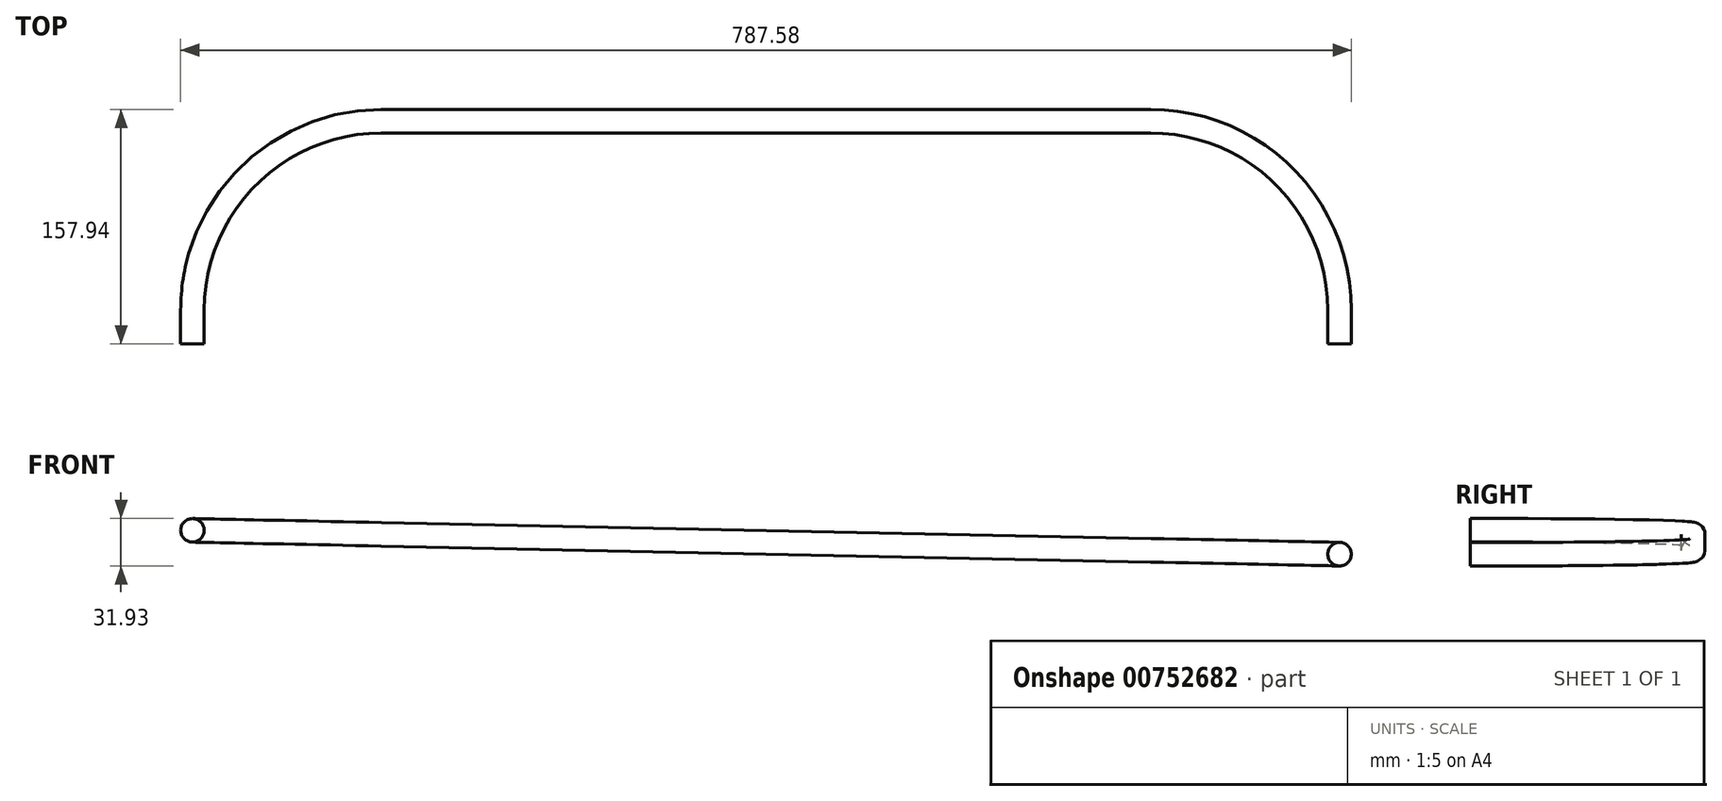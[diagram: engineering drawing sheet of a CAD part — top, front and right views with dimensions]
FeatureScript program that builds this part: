
annotation { "Feature Type Name" : "Feature", "Feature Type Description" : "" }
export const myFeature = defineFeature(function(context is Context, id is Id, definition is map)
    precondition{}
    {
        {
            var Q0;
            Q0=qCreatedBy(makeId("Front.planeOp"),FACE);
            var sketch = newSketch(context, id + "F0", { "sketchPlane" : qUnion([Q0])});
            skLineSegment(sketch, "E0", {"start": v(0, 0) * mm, "end": v(-771.7, 0) * mm, "construction": true});
            skLineSegment(sketch, "E1", {"start": v(-771.7, 0) * mm, "end": v(-771.7, 16.05) * mm, "construction": true});
            skPoint(sketch, "E2", {"position": v(-771.7, 16.05) * mm});
            skLineSegment(sketch, "E3", {"start": v(0, 0) * mm, "end": v(-771.7, 16.05) * mm});
            skSolve(sketch);
        }
        {
            var Q0;
            Q0=qCreatedBy(makeId("Top.planeOp"),FACE);
            var sketch = newSketch(context, id + "F1", { "sketchPlane" : qUnion([Q0])});
            skLineSegment(sketch, "E4", {"start": v(0, 0) * mm, "end": v(0, -50) * mm});
            skSolve(sketch);
        }
        {
            var Q0;
            Q0=sQuery(id+"F1.wireOp",VERTEX,"E4.end");
            var Q1;
            Q1=sQuery(id+"F0.wireOp",VERTEX,"E0.start");
            var Q2;
            Q2=sQuery(id+"F0.wireOp",VERTEX,"E2");
            cPlane(context, id + "F2", {"entities" : qUnion([Q0, Q1, Q2]), "cplaneType" : CPlaneType.THREE_POINT, "offset" : 16.05 * mm, "width" : 150 * mm, "height" : 150 * mm});
        }
        {
            var Q0;
            Q0=qCreatedBy(id+"F2.planeOp",FACE);
            var sketch = newSketch(context, id + "F3", { "sketchPlane" : qUnion([Q0])});
            skLineSegment(sketch, "E5", {"start": v(-771.87, 127) * mm, "end": v(-771.87, 150) * mm});
            skLineSegment(sketch, "E6", {"start": v(-644.87, 0) * mm, "end": v(-127, 0) * mm});
            skPoint(sketch, "E7.visualSharp", {"position": v(0, 0) * mm});
            skArc(sketch, "E7.filletArc", {"start": v(-127, 0) * mm, "mid": v(-37.2, 37.2) * mm, "end": v(0, 127) * mm});
            skPoint(sketch, "E8.visualSharp", {"position": v(-771.87, 0) * mm});
            skArc(sketch, "E8.filletArc", {"start": v(-771.87, 127) * mm, "mid": v(-734.67, 37.2) * mm, "end": v(-644.87, 0) * mm});
            skLineSegment(sketch, "E9", {"start": v(0, 127) * mm, "end": v(0, 150) * mm});
            skSolve(sketch);
        }
        {
            var Q0;
            Q0=qCreatedBy(makeId("Front.planeOp"),FACE);
            cPlane(context, id + "F4", {"entities" : qUnion([Q0]), "cplaneType" : CPlaneType.OFFSET, "offset" : 150 * mm, "width" : 150 * mm, "height" : 150 * mm});
        }
        {
            var Q0;
            Q0=qCreatedBy(id+"F4.planeOp",FACE);
            var sketch = newSketch(context, id + "F5", { "sketchPlane" : qUnion([Q0])});
            skCircle(sketch, "E10", {"center": v(0, 0) * mm, "radius": 7.94 * mm});
            skSolve(sketch);
        }
        {
            var Q0;
            Q0 = qSketchRegion(id + "F5", true);
            var Q1;
            Q1 = qConstructionFilter(qBodyType(qCreatedBy(id + "F3" ,EDGE), BodyType.WIRE), ConstructionObject.NO);
            sweep(context, id + "F6", {"profiles" : qUnion([Q0]), "path" : qUnion([Q1])});
        }
    });
